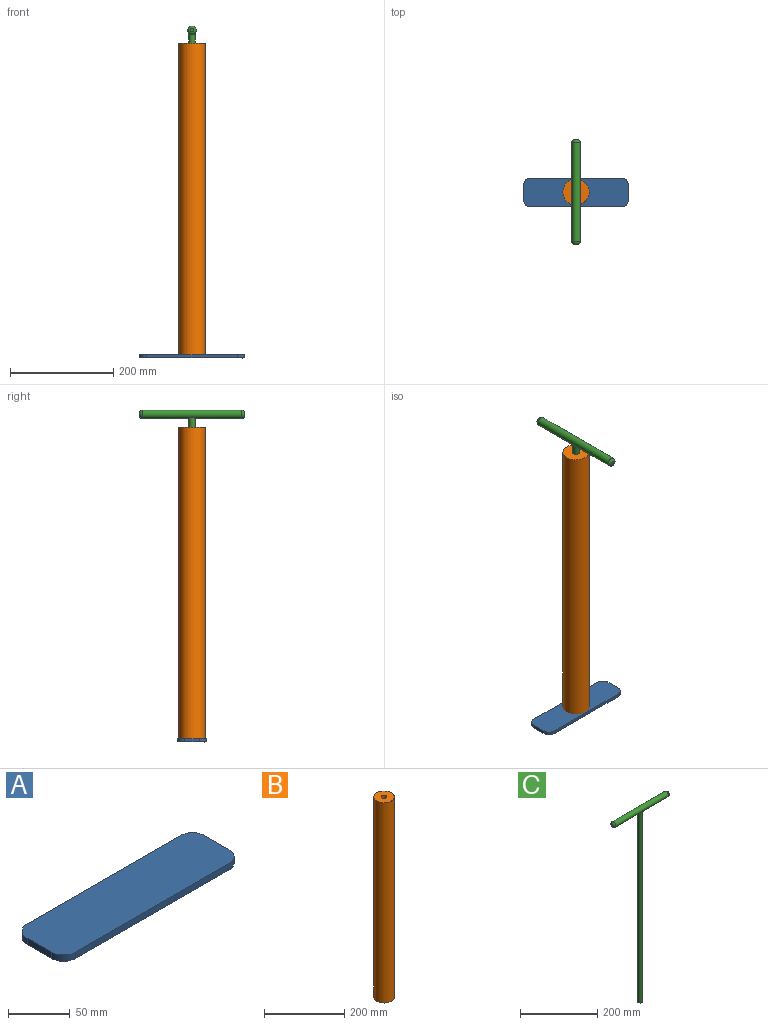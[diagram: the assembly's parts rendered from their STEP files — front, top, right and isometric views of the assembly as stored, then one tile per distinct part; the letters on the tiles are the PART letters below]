
ASSEMBLY  parts=3 mates=2
PART A: 10 faces, bbox 203.2x55.9x6.4 mm
  f0: plane 175.17x6.35mm, normal (0,1,0), area 1112.4mm2, adj f1,f7,f8,f9
  f1: cylinder r=14.01mm len=14.01mm, axis (0,0,-1), area 139.8mm2, adj f0,f2,f8,f9
  f2: plane 27.85x6.35mm, normal (-1,0,0), area 176.9mm2, adj f1,f3,f8,f9
  f3: cylinder r=14.01mm len=14.01mm, axis (0,0,-1), area 139.8mm2, adj f2,f4,f8,f9
  f4: plane 175.17x6.35mm, normal (0,-1,0), area 1112.4mm2, adj f3,f5,f8,f9
  f5: cylinder r=14.01mm len=14.01mm, axis (0,0,-1), area 139.8mm2, adj f4,f6,f8,f9
  f6: plane 27.85x6.35mm, normal (1,0,0), area 176.9mm2, adj f5,f7,f8,f9
  f7: cylinder r=14.01mm len=14.01mm, axis (0,0,-1), area 139.8mm2, adj f0,f6,f8,f9
  f8: plane 203.2x55.88mm, normal (0,0,1), area 11186.3mm2, adj f0,f1,f2,f3,f4,f5,f6,f7
  f9: plane 203.2x55.88mm, normal (0,0,-1), area 11186.3mm2, adj f0,f1,f2,f3,f4,f5,f6,f7
PART B: 4 faces, bbox 50.8x50.8x609.6 mm
  f0: cylinder r=25.4mm len=609.6mm, axis (0,0,-1), area 97287.8mm2, adj f1,f2
  f1: plane 50.8x50.8mm, normal (0,0,1), area 1883.9mm2, adj f0,f3
  f2: plane 50.8x50.8mm, normal (0,0,-1), area 1883.9mm2, adj f0,f3
  f3: cylinder r=6.75mm len=609.6mm, axis (0,0,-1), area 25839.6mm2, adj f1,f2
PART C: 9 faces, bbox 203.2x16.5x617.9 mm
  f0: plane 6.35x6.35mm, normal (1,0,0), area 31.7mm2, adj f1
  f1: torus R=3.17mm, axis (1,0,0), area 321.3mm2, adj f0,f2
  f2: cylinder r=8.26mm len=193.04mm, axis (1,0,0), area 9873.3mm2, adj f1,f3,f5
  f3: torus R=3.17mm, axis (1,0,0), area 321.3mm2, adj f2,f4
  f4: plane 6.35x6.35mm, normal (-1,0,0), area 31.7mm2, adj f3
  f5: cylinder r=6.35mm len=604.33mm, axis (0,0,1), area 24048.8mm2, adj f2,f6
  f6: plane 12.7x12.7mm, normal (0,0,-1), area 126.7mm2, adj f5
  f7: sphere r=6.35mm, area 253.4mm2, adj f8
  f8: plane 12.7x12.7mm, normal (0,0,1), area 126.7mm2, adj f7
PLACE A rot(axis=(0.6,0.59,0.55),0deg) t=(28.78,1.73,-70.59)mm
PLACE B rot(axis=(0.6,0.59,0.55),0deg) t=(28.78,1.73,-70.59)mm
PLACE C rot(axis=(0,0,1),90deg) t=(59.63,212.98,564.41)mm
MATE fastened A.f9 <-> B.f0  axis (0,0,-1) through (28.78,1.73,-70.59)mm
MATE slider C.f5 <-> B.f3  axis (0,0,-1) through (28.78,1.73,-45.19)mm
